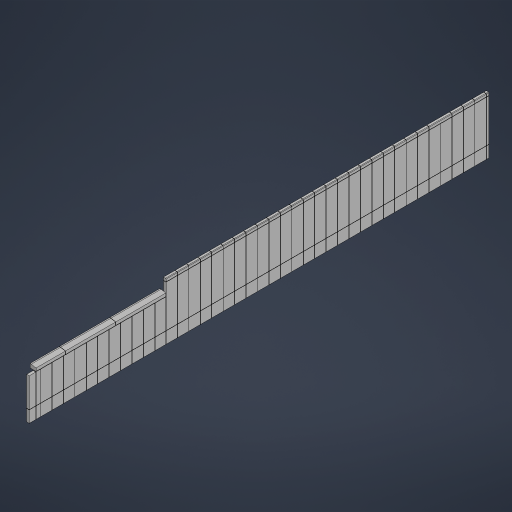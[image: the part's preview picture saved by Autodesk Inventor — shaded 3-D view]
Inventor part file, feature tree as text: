
AUTODESK INVENTOR PART (.ipt)
format: ipt  version: 2023.1 (Build 271208000, 208)  size: 625,664 bytes
history: native  units: in
note: dims shown in document units (in); Inventor stores cm internally (conversion verified against a paired STEP export)
features: other x106, sketch x1, extrude x1
ambient origin geometry x8: Origin, YZ Plane, XZ Plane, XY Plane, X Axis, Y Axis, Z Axis, Center Point
bodies: Solid234 (feature_tree), Solid235 (feature_tree), Solid236 (feature_tree), Solid237 (feature_tree), Solid238 (feature_tree), Solid239 (feature_tree), Solid240 (feature_tree), Solid241 (feature_tree), Solid242 (feature_tree), Solid243 (feature_tree), Solid244 (feature_tree), Solid245 (feature_tree), Solid246 (feature_tree), Solid247 (feature_tree), Solid248 (feature_tree), Solid249 (feature_tree), Solid250 (feature_tree), Solid251 (feature_tree), Solid252 (feature_tree), Solid253 (feature_tree), Solid254 (feature_tree), Solid255 (feature_tree), Solid256 (feature_tree), Solid257 (feature_tree), Solid258 (feature_tree), Solid259 (feature_tree), Solid260 (feature_tree), Solid261 (feature_tree), Solid262 (feature_tree), Solid263 (feature_tree), Solid264 (feature_tree), Solid265 (feature_tree), Solid266 (feature_tree), Solid267 (feature_tree), Solid268 (feature_tree), Solid269 (feature_tree), Solid270 (feature_tree), Solid271 (feature_tree), Solid272 (feature_tree), Solid273 (feature_tree), Solid274 (feature_tree), Solid275 (feature_tree), Solid276 (feature_tree), Solid277 (feature_tree), Solid278 (feature_tree), Solid279 (feature_tree), Solid280 (feature_tree), Solid281 (feature_tree), Solid282 (feature_tree), Solid283 (feature_tree), Solid284 (feature_tree), Solid285 (feature_tree), Solid286 (feature_tree), Solid287 (feature_tree), Solid288 (feature_tree), Solid289 (feature_tree), Solid290 (feature_tree), Solid291 (feature_tree), Solid292 (feature_tree), Solid294 (feature_tree), Solid295 (feature_tree), Solid296 (feature_tree), Solid297 (feature_tree), Solid298 (feature_tree), Solid299 (feature_tree), Solid300 (feature_tree), Solid301 (feature_tree), Solid302 (feature_tree), Solid303 (feature_tree), Solid304 (feature_tree), Solid305 (feature_tree), Solid306 (feature_tree), Solid307 (feature_tree), Solid308 (feature_tree), Solid309 (feature_tree), Solid310 (feature_tree), Solid311 (feature_tree), Solid312 (feature_tree), Solid313 (feature_tree), Solid314 (feature_tree), Solid315 (feature_tree), Solid316 (feature_tree), Solid317 (feature_tree), Solid318 (feature_tree), Solid319 (feature_tree), Solid320 (feature_tree), Solid529 (feature_tree), Solid530 (feature_tree), Solid531 (feature_tree), Solid532 (feature_tree), Solid533 (feature_tree), Solid534 (feature_tree), Solid535 (feature_tree), Solid536 (feature_tree), Solid537 (feature_tree), Solid538 (feature_tree), Solid539 (feature_tree), Solid540 (feature_tree), Solid541 (feature_tree), Solid542 (feature_tree), Solid543 (feature_tree), Solid544 (feature_tree), Solid545 (feature_tree), Solid546 (feature_tree), Solid547 (feature_tree), Solid548 (feature_tree), Solid549 (feature_tree), Solid550 (feature_tree), Solid551 (feature_tree), Solid552 (feature_tree), Solid553 (feature_tree), Solid554 (feature_tree), Solid555 (feature_tree), Solid556 (feature_tree)
feature tree (108):
  other  "SE13 (15)"
  sketch  "Sketch2"  dims[d3=12.625in d4=0.0in]
  extrude  "Extrusion1"  [1 undecoded]
  other  "SE13"
  other  "SE1 (1)"
  other  "SE1 (2)"
  other  "SE1 (3)"
  other  "SE1 (4)"
  other  "SE1 (5)"
  other  "SE1 (6)"
  other  "SE1 (7)"
  other  "SE1 (8)"
  other  "SE1 (9)"
  other  "SE1 (10)"
  other  "SE1 (11)"
  other  "SE1 (12)"
  other  "SE1 (13)"
  other  "SE1 (14)"
  other  "SE1 (15)"
  other  "SE1 (16)"
  other  "SE1 (17)"
  other  "SE1 (18)"
  other  "SE1 (19)"
  other  "SE1 (20)"
  other  "SE1 (21)"
  other  "SE1 (22)"
  other  "SE1 (23)"
  other  "SE1 (24)"
  other  "SE1 (25)"
  other  "SE1 (26)"
  other  "SE1 (27)"
  other  "SE7 (28)"
  other  "SE7 (1)"
  other  "SE7 (2)"
  other  "SE7 (3)"
  other  "SE7 (4)"
  other  "SE7 (5)"
  other  "SE7 (6)"
  other  "SE7 (7)"
  other  "SE7 (8)"
  other  "SE7 (9)"
  other  "SE7 (10)"
  other  "SE7 (11)"
  other  "SE7 (12)"
  other  "SE7 (13)"
  other  "SE7 (27)"
  other  "SE7 (14)"
  other  "SE7 (15)"
  other  "SE7 (16)"
  other  "SE7 (17)"
  other  "SE7 (18)"
  other  "SE7 (19)"
  other  "SE7 (20)"
  other  "SE7 (21)"
  other  "SE7 (22)"
  other  "SE7 (23)"
  other  "SE7 (24)"
  other  "SE7 (25)"
  other  "SE7 (26)"
  other  "SE3 (1)"
  other  "SE3 (2)"
  other  "SE3 (3)"
  other  "SE3 (4)"
  other  "SE3 (5)"
  other  "SE3 (6)"
  other  "SE3 (7)"
  other  "SE3 (8)"
  other  "SE3 (9)"
  other  "SE9 (1)"
  other  "SE9 (2)"
  other  "SE9 (3)"
  other  "SE9 (4)"
  other  "SE11"
  other  "SE9 (5)"
  other  "SE9 (6)"
  other  "SE9 (7)"
  other  "SE9 (8)"
  other  "SE9 (9)"
  other  "SE12"
  other  "SE15"
  other  "SE10"
  other  "SE13 (1)"
  other  "SE13 (2)"
  other  "SE13 (3)"
  other  "SE13 (4)"
  other  "SE13 (5)"
  other  "SE13 (6)"
  other  "SE13 (7)"
  other  "SE13 (8)"
  other  "SE13 (9)"
  other  "SE13 (10)"
  other  "SE13 (11)"
  other  "SE13 (12)"
  other  "SE13 (13)"
  other  "SE13 (14)"
  other  "SE13 (16)"
  other  "SE13 (17)"
  other  "SE13 (18)"
  other  "SE13 (19)"
  other  "SE13 (20)"
  other  "SE13 (21)"
  other  "SE13 (22)"
  other  "SE13 (23)"
  other  "SE14"
  other  "SE13 (25)"
  other  "SE13 (26)"
  other  "SE15 (1)"
  other  "SE16"
note: 1 required parameter value undecoded (feature->parameter linkage not recoverable at this tier; creation-order binding heuristic only, values carry confidence <= 0.55)
